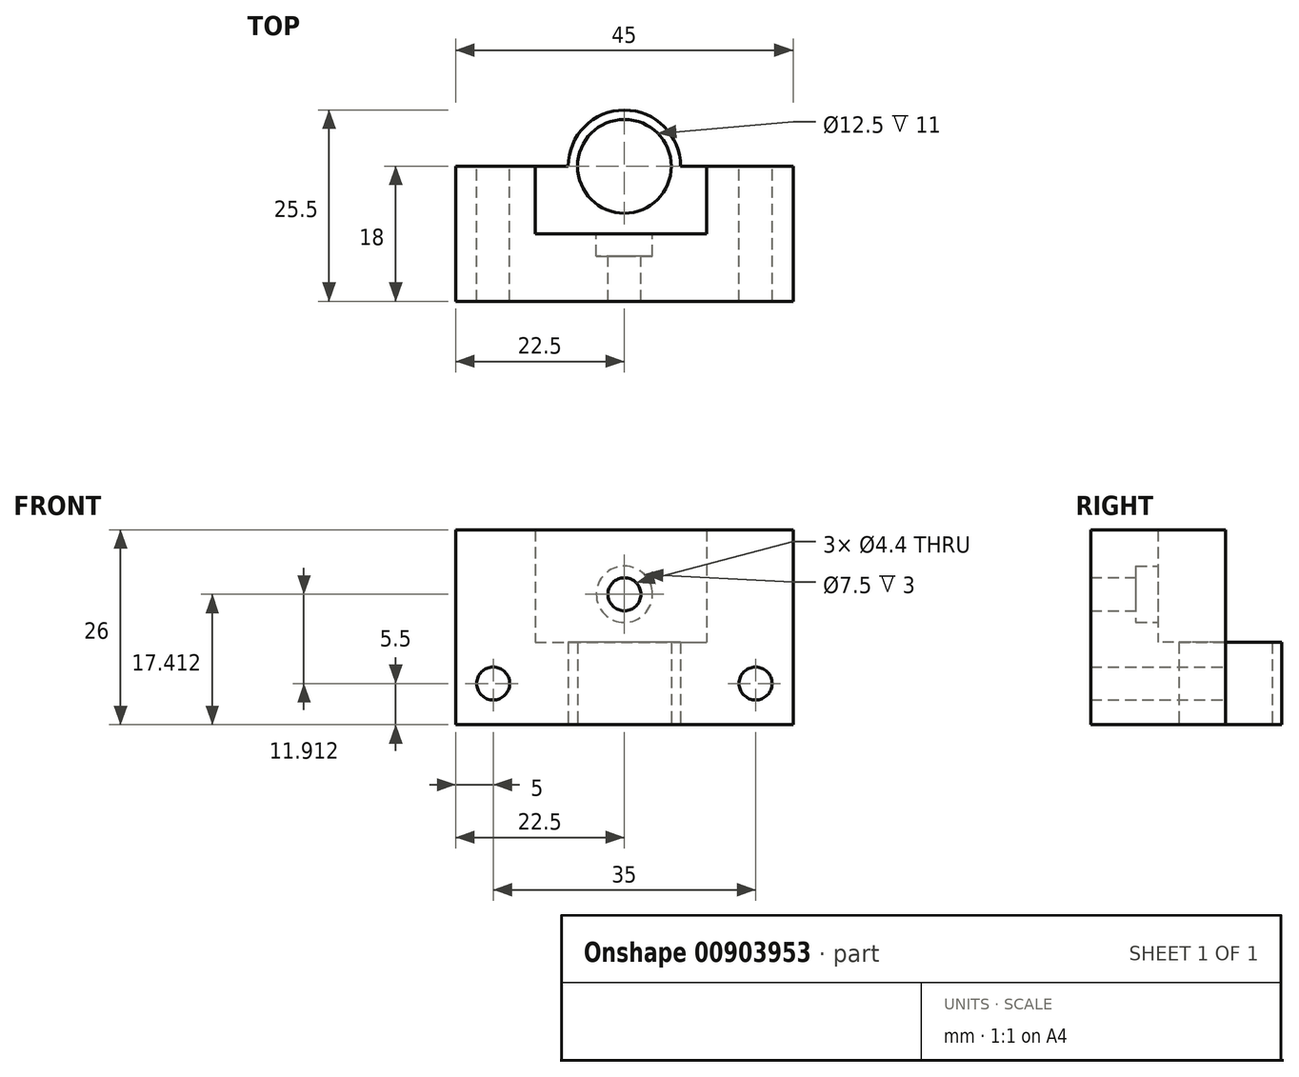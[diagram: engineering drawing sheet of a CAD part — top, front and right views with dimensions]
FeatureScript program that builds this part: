
annotation { "Feature Type Name" : "Feature", "Feature Type Description" : "" }
export const myFeature = defineFeature(function(context is Context, id is Id, definition is map)
    precondition{}
    {
        {
            var Q0;
            Q0=qCreatedBy(makeId("Top.planeOp"),FACE);
            var sketch = newSketch(context, id + "F0", { "sketchPlane" : qUnion([Q0])});
            skLineSegment(sketch, "E0.bottom", {"start": v(-22.5, 9) * mm, "end": v(-7.5, 9) * mm});
            skLineSegment(sketch, "E0.top", {"start": v(-22.5, -9) * mm, "end": v(22.5, -9) * mm});
            skLineSegment(sketch, "E0.left", {"start": v(-22.5, 9) * mm, "end": v(-22.5, -9) * mm});
            skLineSegment(sketch, "E0.right", {"start": v(22.5, 9) * mm, "end": v(22.5, -9) * mm});
            skPoint(sketch, "E0.middle", {"position": v(0, 0) * mm});
            skCircle(sketch, "E1", {"center": v(0, 9) * mm, "radius": 7.5 * mm});
            skCircle(sketch, "E2", {"center": v(0, 9) * mm, "radius": 6.25 * mm});
            skLineSegment(sketch, "E3.trimOffspring", {"start": v(7.5, 9) * mm, "end": v(22.5, 9) * mm});
            skSolve(sketch);
        }
        {
            var Q0;
            {var subQ0=sQuery(id+"F0.wireOp",EDGE,"E0.bottom");Q0=makeQuery(id+"F0.imprint","IMPRINT",FACE,{"disambiguationData":[TD([[makeQuery(id+"F0.imprint","IMPRINT",EDGE,{"derivedFrom":subQ0}),-1.0]])]});}
            var Q1;
            Q1=makeQuery(id+"F0.imprint","IMPRINT",FACE,{"disambiguationData":[TD([[makeQuery(id+"F0.imprint","IMPRINT",EDGE,{"derivedFrom":sQuery(id+"F0.wireOp",EDGE,"E2")}),-1.0]])]});
            extrude(context, id + "F1", {"entities" : qUnion([Q0, Q1]), "depth" : 11 * mm, "offsetDistance" : 25 * mm});
        }
        {
            var Q0;
            Q0=makeQuery(id+"F1.opExtrude","SWEPT_FACE",FACE,{"disambiguationData":[OSD([sQuery(id+"F0.wireOp",EDGE,"E3.trimOffspring")])]});
            var sketch = newSketch(context, id + "F2", { "sketchPlane" : qUnion([Q0])});
            skCircle(sketch, "E4", {"center": v(-17.5, 5.5) * mm, "radius": 2.2 * mm});
            skPoint(sketch, "E4.centerSnap0", {"position": v(-22.5, 5.5) * mm});
            skCircle(sketch, "E5", {"center": v(17.5, 5.5) * mm, "radius": 2.2 * mm});
            skSolve(sketch);
        }
        {
            var Q0;
            Q0=makeQuery(id+"F2.imprint","IMPRINT",FACE,{"disambiguationData":[TD([[makeQuery(id+"F2.imprint","IMPRINT",EDGE,{"derivedFrom":sQuery(id+"F2.wireOp",EDGE,"E5")}),1.0]])]});
            var Q1;
            Q1=makeQuery(id+"F2.imprint","IMPRINT",FACE,{"disambiguationData":[TD([[makeQuery(id+"F2.imprint","IMPRINT",EDGE,{"derivedFrom":sQuery(id+"F2.wireOp",EDGE,"E4")}),1.0]])]});
            extrude(context, id + "F3", {"entities" : qUnion([Q0, Q1]), "operationType" : NewBodyOperationType.REMOVE, "endBound" : BoundingType.THROUGH_ALL, "oppositeDirection" : true, "depth" : 25 * mm, "offsetDistance" : 25 * mm});
        }
        {
            var Q0;
            Q0=makeQuery(id+"F1.opExtrude","CAP_FACE",FACE,{"disambiguationData":[OSD([sQuery(id+"F0.wireOp",EDGE,"E0.bottom"),sQuery(id+"F0.wireOp",EDGE,"E0.top"),sQuery(id+"F0.wireOp",EDGE,"E0.left"),sQuery(id+"F0.wireOp",EDGE,"E0.right"),sQuery(id+"F0.wireOp",EDGE,"E1"),sQuery(id+"F0.wireOp",EDGE,"E2"),sQuery(id+"F0.wireOp",EDGE,"E3.trimOffspring")])],"isStart":false});
            var sketch = newSketch(context, id + "F4", { "sketchPlane" : qUnion([Q0])});
            skLineSegment(sketch, "E6", {"start": v(-22.5, 9) * mm, "end": v(-22.5, -9) * mm});
            skLineSegment(sketch, "E7", {"start": v(-22.5, -9) * mm, "end": v(22.5, -9) * mm});
            skLineSegment(sketch, "E8", {"start": v(22.5, -9) * mm, "end": v(22.5, 9) * mm});
            skLineSegment(sketch, "E9", {"start": v(22.5, 9) * mm, "end": v(10.98, 9) * mm});
            skLineSegment(sketch, "E10", {"start": v(10.98, 9) * mm, "end": v(10.98, 0) * mm});
            skLineSegment(sketch, "E11", {"start": v(-11.91, 9) * mm, "end": v(-11.91, 0) * mm});
            skLineSegment(sketch, "E12", {"start": v(-11.91, 0) * mm, "end": v(10.98, 0) * mm});
            skPoint(sketch, "E13.orphan", {"position": v(-11.91, -9) * mm});
            skPoint(sketch, "E14.orphan", {"position": v(10.98, -9) * mm});
            skSolve(sketch);
        }
        {
            var Q0;
            {var subQ0=sQuery(id+"F4.wireOp",EDGE,"E6");Q0=makeQuery(id+"F4.imprint","IMPRINT",FACE,{"disambiguationData":[TD([[makeQuery(id+"F4.imprint","IMPRINT",EDGE,{"derivedFrom":subQ0}),1.0]])]});}
            extrude(context, id + "F5", {"entities" : qUnion([Q0]), "operationType" : NewBodyOperationType.ADD, "depth" : 15 * mm, "offsetDistance" : 25 * mm});
        }
        {
            var Q0;
            Q0=makeQuery(id+"F5.opExtrude","SWEPT_FACE",FACE,{"disambiguationData":[OSD([sQuery(id+"F4.wireOp",EDGE,"E12")])]});
            var sketch = newSketch(context, id + "F6", { "sketchPlane" : qUnion([Q0])});
            skCircle(sketch, "E15", {"center": v(0, 17.41) * mm, "radius": 2.2 * mm});
            skCircle(sketch, "E16", {"center": v(0, 17.41) * mm, "radius": 3.75 * mm});
            skSolve(sketch);
        }
        {
            var Q0;
            Q0=makeQuery(id+"F6.imprint","IMPRINT",FACE,{"disambiguationData":[TD([[makeQuery(id+"F6.imprint","IMPRINT",EDGE,{"derivedFrom":sQuery(id+"F6.wireOp",EDGE,"E15")}),-1.0]])]});
            extrude(context, id + "F7", {"entities" : qUnion([Q0]), "operationType" : NewBodyOperationType.REMOVE, "oppositeDirection" : true, "depth" : 3 * mm, "offsetDistance" : 25 * mm});
        }
        {
            var Q0;
            Q0=makeQuery(id+"F7.boolean.opBoolean","SPLIT",FACE,{"disambiguationData":[TD([makeQuery(id+"F7.opExtrude","SWEPT_FACE",FACE,{"disambiguationData":[OSD([sQuery(id+"F6.wireOp",EDGE,"E15")])]})])],"derivedFrom":makeQuery(id+"F5.opExtrude","SWEPT_FACE",FACE,{"disambiguationData":[OSD([sQuery(id+"F4.wireOp",EDGE,"E12")])]})});
            extrude(context, id + "F8", {"entities" : qUnion([Q0]), "operationType" : NewBodyOperationType.REMOVE, "endBound" : BoundingType.THROUGH_ALL, "oppositeDirection" : true, "depth" : 25 * mm, "offsetDistance" : 25 * mm});
        }
    });
